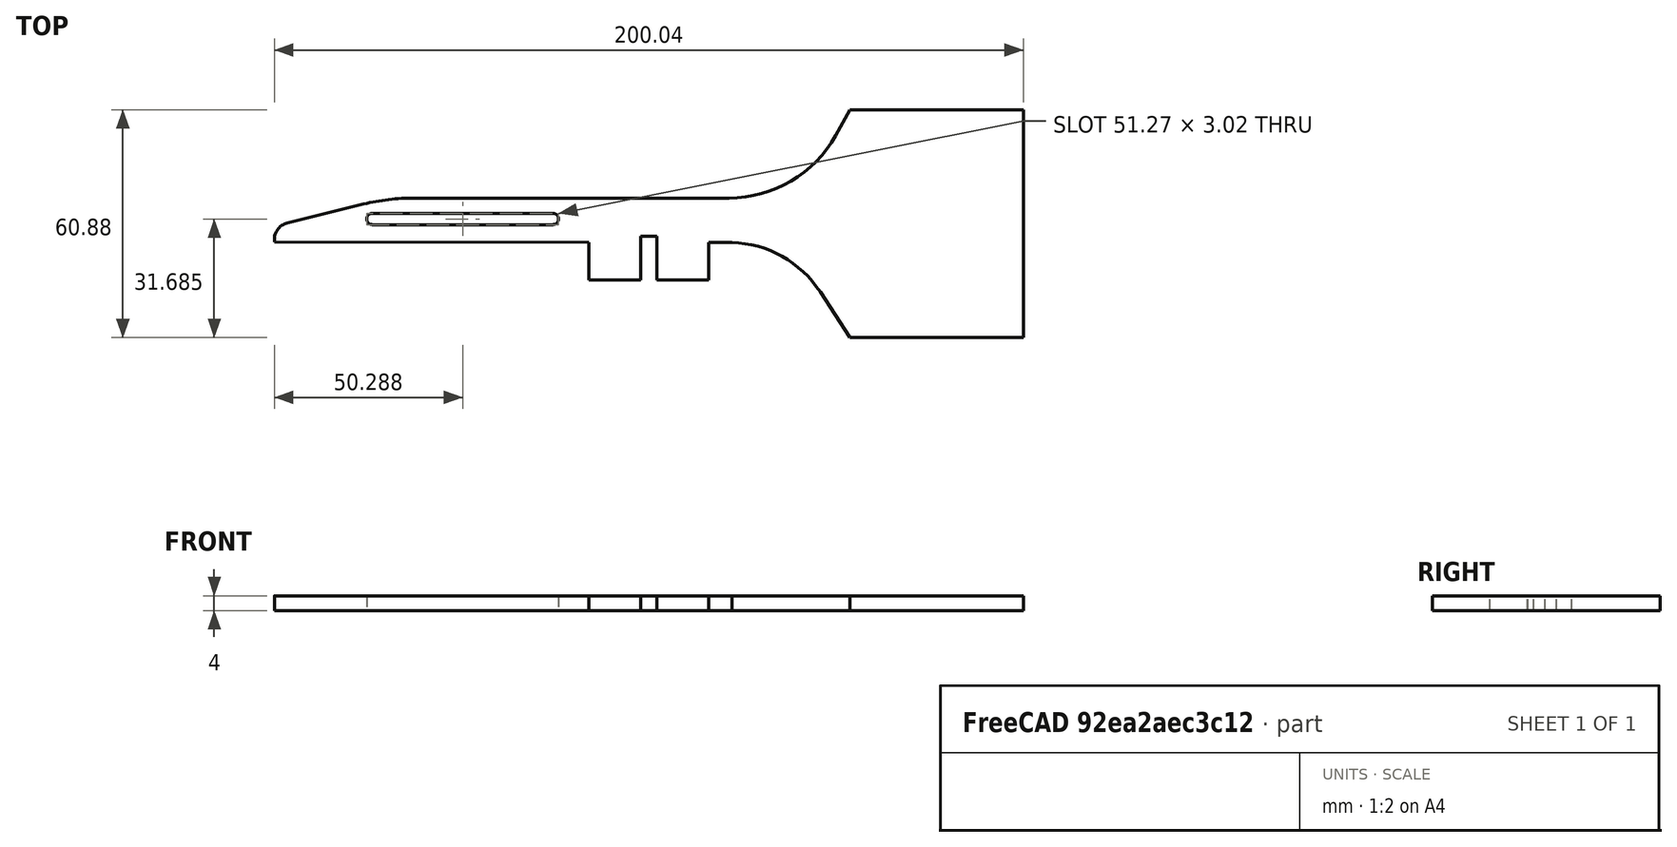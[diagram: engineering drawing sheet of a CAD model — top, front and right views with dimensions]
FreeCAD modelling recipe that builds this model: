
FCSTD DOCUMENT  (FreeCAD 0.18R16131 (Git))
Label: solo_banderuola4mm_v2
License: All rights reserved
LicenseURL: http://en.wikipedia.org/wiki/All_rights_reserved
objects: Sketcher::SketchObject×1, PartDesign::Pad×1, PartDesign::Body×1
note: 4 computed .brp shape members not serialized (recipe doc carries the construction recipe); baked Part::Feature solids carry a one-line shape summary decoded from their .brp

FEATURE [Sketcher::SketchObject] CopySketch004
  sketch-geometry (30):
    g0: LineSegment StartX=-96.5154 StartY=5.23881 StartZ=0 EndX=-76.2174 EndY=10.2337 EndZ=0
    g1: LineSegment StartX=-62.72 StartY=11.87 StartZ=0 EndX=-42.5521 EndY=11.87 EndZ=0
    g2: LineSegment StartX=-42.5521 StartY=11.87 StartZ=0 EndX=21.448 EndY=11.87 EndZ=0
    g3: LineSegment StartX=49.8859 StartY=28.6225 StartZ=0 EndX=53.6734 EndY=35.4564 EndZ=0
    g4: LineSegment StartX=53.6734 StartY=35.4564 StartZ=0 EndX=100 EndY=35.4564 EndZ=0
    g5: LineSegment StartX=100 StartY=35.4564 StartZ=0 EndX=100 EndY=0 EndZ=0
    g6: ArcOfCircle CenterX=-62.72 CenterY=-44.6165 CenterZ=0 NormalX=0 NormalY=0 NormalZ=1 AngleXU=0 Radius=56.4865 StartAngle=1.5708 EndAngle=1.81208
    g7: ArcOfCircle CenterX=21.448 CenterY=44.3835 CenterZ=0 NormalX=0 NormalY=0 NormalZ=1 AngleXU=0 Radius=32.5135 StartAngle=4.71239 EndAngle=5.7771
    g8: ArcOfCircle CenterX=-95.4076 CenterY=0.737112 CenterZ=0 NormalX=0 NormalY=0 NormalZ=1 AngleXU=0 Radius=4.636 StartAngle=1.81208 EndAngle=3.27886
    g9: GeomPoint X=16 Y=7.1e-15 Z=0
    g10: GeomPoint X=-16 Y=0 Z=0
    g11: LineSegment StartX=-16 StartY=0 StartZ=0 EndX=-16 EndY=-10 EndZ=0
    g12: LineSegment StartX=-16 StartY=-10 StartZ=0 EndX=-2.15 EndY=-10 EndZ=0
    g13: LineSegment StartX=16 StartY=-10 StartZ=0 EndX=16 EndY=7.1e-15 EndZ=0
    g14: LineSegment StartX=-16 StartY=2e-16 StartZ=0 EndX=-100 EndY=0.10272 EndZ=0
    g15: GeomPoint X=-2.15 Y=-10 Z=0
    g16: GeomPoint X=2.15 Y=-10 Z=0
    g17: LineSegment StartX=-2.15 StartY=-10 StartZ=0 EndX=-2.15 EndY=1.64739 EndZ=0
    g18: LineSegment StartX=-2.15 StartY=1.64739 StartZ=0 EndX=2.15 EndY=1.64739 EndZ=0
    g19: LineSegment StartX=2.15 StartY=1.64739 StartZ=0 EndX=2.15 EndY=-10 EndZ=0
    g20: LineSegment StartX=2.15 StartY=-10 StartZ=0 EndX=16 EndY=-10 EndZ=0
    g21: ArcOfCircle CenterX=21.288 CenterY=-29.1835 CenterZ=0 NormalX=0 NormalY=0 NormalZ=1 AngleXU=0 Radius=29.1956 StartAngle=0.576891 EndAngle=1.54195
    g22: LineSegment StartX=45.7586 StartY=-13.2596 StartZ=0 EndX=53.6734 EndY=-25.4225 EndZ=0
    g23: LineSegment StartX=53.6734 StartY=-25.4225 StartZ=0 EndX=100 EndY=-25.4225 EndZ=0
    g24: LineSegment StartX=100 StartY=-25.4225 StartZ=0 EndX=100 EndY=0 EndZ=0
    g25: LineSegment StartX=16 StartY=7.1e-15 StartZ=0 EndX=22.1301 EndY=7.1e-15 EndZ=0
    g26: ArcOfCircle CenterX=-73.8787 CenterY=6.26519 CenterZ=0 NormalX=0 NormalY=0 NormalZ=1 AngleXU=0 Radius=1.51 StartAngle=1.5708 EndAngle=4.71239
    g27: ArcOfCircle CenterX=-25.6248 CenterY=6.26519 CenterZ=0 NormalX=0 NormalY=0 NormalZ=1 AngleXU=0 Radius=1.51 StartAngle=4.71239 EndAngle=7.85398
    g28: LineSegment StartX=-73.8787 StartY=4.75519 StartZ=0 EndX=-25.6248 EndY=4.75519 EndZ=0
    g29: LineSegment StartX=-73.8787 StartY=7.77519 StartZ=0 EndX=-25.6248 EndY=7.77519 EndZ=0
  constraints (60):
    c: Horizontal(g1)
    c: Coincident(g1,g2)
    c: Horizontal(g2)
    c: Coincident(g3,g4)
    c: Horizontal(g4)
    c: Coincident(g4,g5)
    c: PointOnObject(g5,g-1)
    c: Vertical(g5)
    c: Tangent(g0,g6) = 1.5708
    c: Tangent(g1,g6) = 1.5708
    c: Tangent(g2,g7) = -1.5708
    c: Tangent(g3,g7) = -1.5708
    c: Tangent(g0,g8) = 1.5708
    c: Coincident(g14,g8) = 1.5708
    c: DistanceX(g14,g5) = 200
    c: DistanceX(g-1,g5) = 100
    c: DistanceX(g10,g9) = 32
    c: Symmetric(g9,g10,g-2)
    c: Coincident(g11,g10)
    c: Vertical(g11)
    c: Coincident(g11,g12)
    c: Horizontal(g12)
    c: Coincident(g20,g13)
    c: Vertical(g13)
    c: Coincident(g13,g9)
    c: PointOnObject(g14,g11)
    c: PointOnObject(g15,g12)
    c: DistanceY(g13,g13) = 10
    c: Symmetric(g15,g16,g-2)
    c: Coincident(g17,g15)
    c: Vertical(g17)
    c: Coincident(g17,g18)
    c: Horizontal(g18)
    c: Coincident(g18,g19)
    c: Coincident(g19,g16)
    c: Vertical(g19)
    c: PointOnObject(g12,g17)
    c: PointOnObject(g20,g19)
    c: Tangent(g12,g20)
    c: DistanceX(g12,g16) = 4.3
    c: Coincident(g22,g23)
    c: Horizontal(g23)
    c: Coincident(g23,g24)
    c: Vertical(g24)
    c: Tangent(g22,g21) = 1.5708
    c: PointOnObject(g9,g-1)
    c: Equal(g4,g23)
    c: Coincident(g24,g5)
    c: Coincident(g25,g9)
    c: Coincident(g25,g21)
    c: Horizontal(g25)
    c: DistanceY(g1) = 11.87
    c: DistanceX(g8,g1) = 37.28
    c: Tangent(g26,g29) = 1.5708
    c: Tangent(g26,g28) = -1.5708
    c: Tangent(g28,g27) = -1.5708
    c: Tangent(g29,g27) = 1.5708
    c: Horizontal(g28)
    c: Equal(g26,g27)
    c: Radius(g27) = 1.51
FEATURE [PartDesign::Pad] Pad
  Length = 4
  Length2 = 100
  Midplane = true
  Profile = -> CopySketch004
  Type = 0
FEATURE [PartDesign::Body] Body001
  Group = -> [Pad]
  Origin = -> Origin001
  Tip = -> Pad
